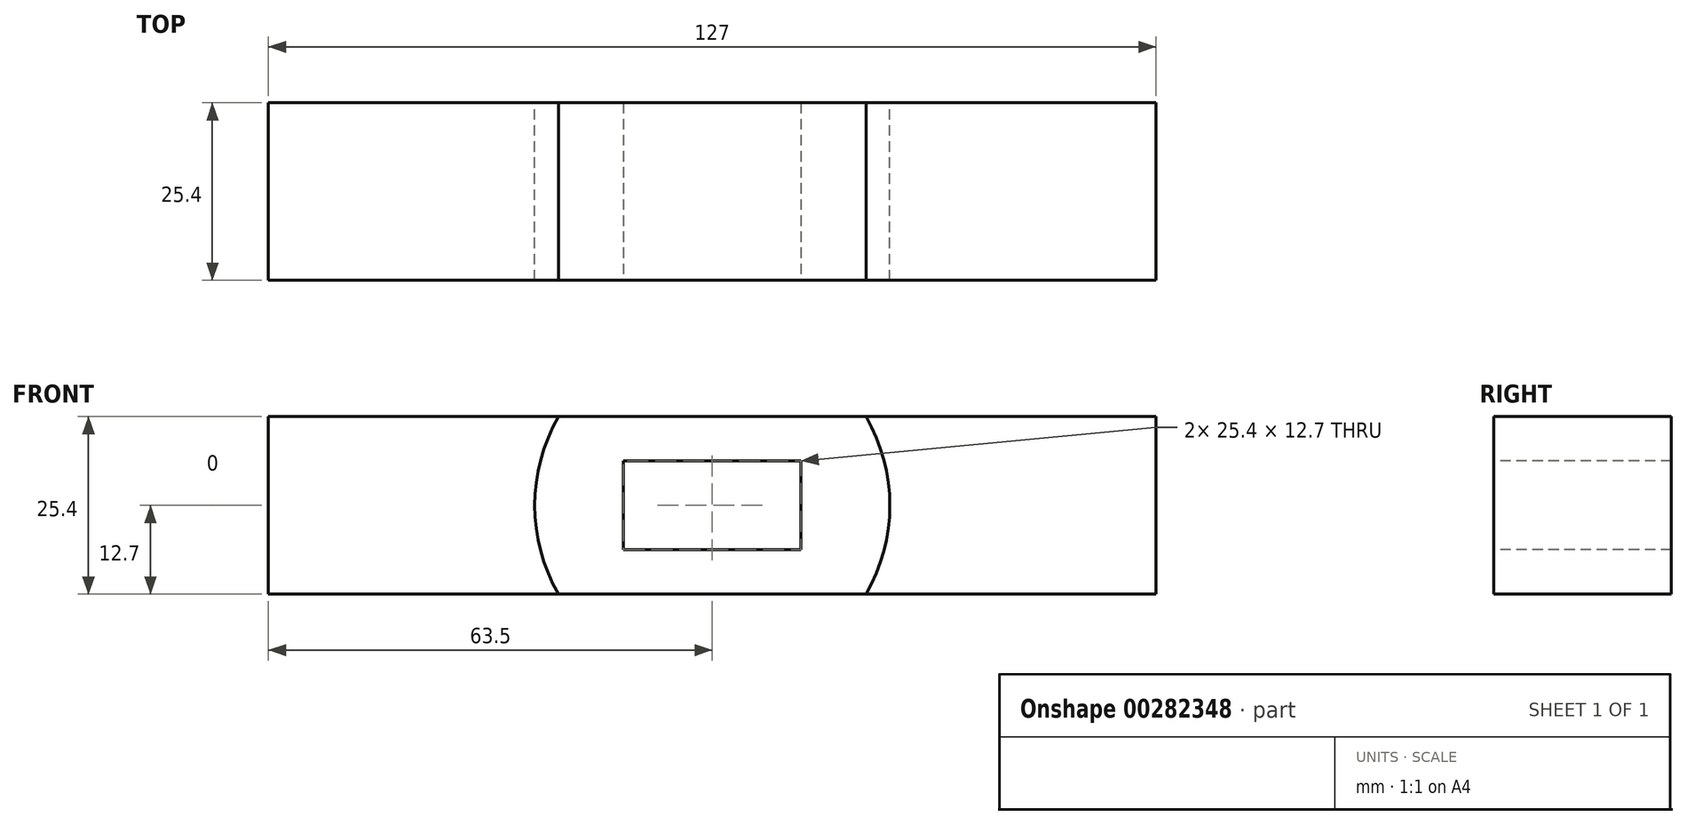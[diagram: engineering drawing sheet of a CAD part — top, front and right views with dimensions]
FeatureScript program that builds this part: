
annotation { "Feature Type Name" : "Feature", "Feature Type Description" : "" }
export const myFeature = defineFeature(function(context is Context, id is Id, definition is map)
    precondition{}
    {
        {
            var Q0;
            Q0=qCreatedBy(makeId("Front.planeOp"),FACE);
            var sketch = newSketch(context, id + "F0", { "sketchPlane" : qUnion([Q0])});
            skLineSegment(sketch, "E0.bottom", {"start": v(63.5, -12.7) * mm, "end": v(-63.5, -12.7) * mm});
            skLineSegment(sketch, "E0.top", {"start": v(63.5, 12.7) * mm, "end": v(-63.5, 12.7) * mm});
            skLineSegment(sketch, "E0.left", {"start": v(63.5, -12.7) * mm, "end": v(63.5, 12.7) * mm});
            skLineSegment(sketch, "E0.right", {"start": v(-63.5, -12.7) * mm, "end": v(-63.5, 12.7) * mm});
            skPoint(sketch, "E0.middle", {"position": v(0, 0) * mm});
            skSolve(sketch);
        }
        {
            var Q0;
            Q0=makeQuery(id+"F0.imprint","IMPRINT",FACE,{"disambiguationData":[TD([[makeQuery(id+"F0.imprint","IMPRINT",EDGE,{"derivedFrom":sQuery(id+"F0.wireOp",EDGE,"E0.bottom")}),-1.0]])]});
            var sketch = newSketch(context, id + "F1", { "sketchPlane" : qUnion([Q0])});
            skCircle(sketch, "E1", {"center": v(0, 0) * mm, "radius": 25.4 * mm});
            skSolve(sketch);
        }
        {
            var Q0;
            Q0=makeQuery(id+"F0.imprint","IMPRINT",FACE,{"disambiguationData":[TD([[makeQuery(id+"F0.imprint","IMPRINT",EDGE,{"derivedFrom":sQuery(id+"F0.wireOp",EDGE,"E0.bottom")}),-1.0]])]});
            var Q1;
            {var subQ0=sQuery(id+"F1.wireOp",EDGE,"E1");var subQ1=makeQuery(id+"F0.imprint","IMPRINT",EDGE,{"derivedFrom":sQuery(id+"F0.wireOp",EDGE,"E0.top")});var subQ2=makeQuery(id+"F1.imprint","INTERSECT",VERTEX,{"disambiguationData":[OD(0.0)],"derivedFrom":[subQ1,subQ0]});Q1=makeQuery(id+"F1.imprint","IMPRINT",FACE,{"disambiguationData":[TD([[makeQuery(id+"F1.imprint","IMPRINT",EDGE,{"disambiguationData":[TD([[subQ2,1.0]])],"derivedFrom":subQ0}),1.0]])]});}
            var Q2;
            {var subQ0=sQuery(id+"F1.wireOp",EDGE,"E1");var subQ1=makeQuery(id+"F0.imprint","IMPRINT",EDGE,{"derivedFrom":sQuery(id+"F0.wireOp",EDGE,"E0.bottom")});var subQ2=makeQuery(id+"F1.imprint","INTERSECT",VERTEX,{"disambiguationData":[OD(0.0)],"derivedFrom":[subQ1,subQ0]});Q2=makeQuery(id+"F1.imprint","IMPRINT",FACE,{"disambiguationData":[TD([[makeQuery(id+"F1.imprint","IMPRINT",EDGE,{"disambiguationData":[TD([[subQ2,-1.0]])],"derivedFrom":subQ0}),1.0]])]});}
            extrude(context, id + "F2", {"entities" : qUnion([Q0, Q1, Q2]), "depth" : 25.4 * mm});
        }
        {
            var Q0;
            Q0=makeQuery(id+"F2.opExtrude","CAP_FACE",FACE,{"disambiguationData":[OSD([sQuery(id+"F0.wireOp",EDGE,"E0.bottom"),sQuery(id+"F0.wireOp",EDGE,"E0.top"),sQuery(id+"F0.wireOp",EDGE,"E0.left"),sQuery(id+"F0.wireOp",EDGE,"E0.right")])],"isStart":false});
            var sketch = newSketch(context, id + "F3", { "sketchPlane" : qUnion([Q0])});
            skLineSegment(sketch, "E2.bottom", {"start": v(12.7, -6.35) * mm, "end": v(-12.7, -6.35) * mm});
            skLineSegment(sketch, "E2.top", {"start": v(12.7, 6.35) * mm, "end": v(-12.7, 6.35) * mm});
            skLineSegment(sketch, "E2.left", {"start": v(12.7, -6.35) * mm, "end": v(12.7, 6.35) * mm});
            skLineSegment(sketch, "E2.right", {"start": v(-12.7, -6.35) * mm, "end": v(-12.7, 6.35) * mm});
            skPoint(sketch, "E2.middle", {"position": v(0, 0) * mm});
            skSolve(sketch);
        }
        {
            var Q0;
            Q0 = qSketchRegion(id + "F3", true);
            extrude(context, id + "F4", {"entities" : qUnion([Q0]), "operationType" : NewBodyOperationType.REMOVE, "oppositeDirection" : true, "depth" : 25.4 * mm});
        }
    });
